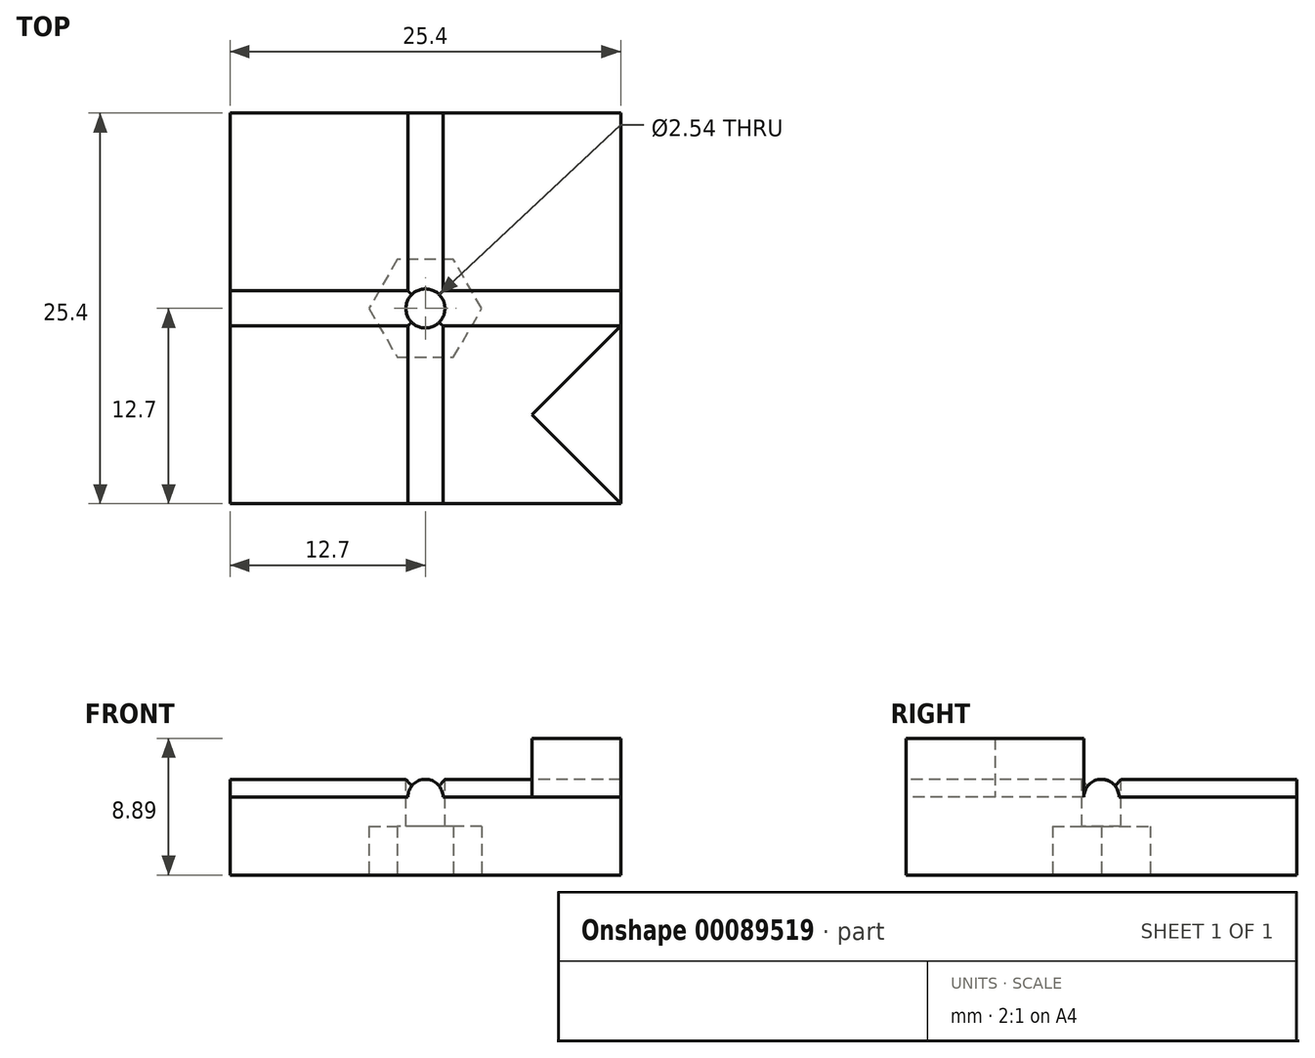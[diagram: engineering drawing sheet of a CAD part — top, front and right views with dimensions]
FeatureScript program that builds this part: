
annotation { "Feature Type Name" : "Feature", "Feature Type Description" : "" }
export const myFeature = defineFeature(function(context is Context, id is Id, definition is map)
    precondition{}
    {
        {
            var Q0;
            Q0=qCreatedBy(makeId("Top.planeOp"),FACE);
            var sketch = newSketch(context, id + "F0", { "sketchPlane" : qUnion([Q0])});
            skLineSegment(sketch, "E0.bottom", {"start": v(12.7, 12.7) * mm, "end": v(-12.7, 12.7) * mm});
            skLineSegment(sketch, "E0.top", {"start": v(12.7, -12.7) * mm, "end": v(-12.7, -12.7) * mm});
            skLineSegment(sketch, "E0.left", {"start": v(12.7, 12.7) * mm, "end": v(12.7, -12.7) * mm});
            skLineSegment(sketch, "E0.right", {"start": v(-12.7, 12.7) * mm, "end": v(-12.7, -12.7) * mm});
            skPoint(sketch, "E0.middle", {"position": v(0, 0) * mm});
            skSolve(sketch);
        }
        {
            var Q0;
            Q0=makeQuery(id+"F0.imprint","IMPRINT",FACE,{"disambiguationData":[TD([[makeQuery(id+"F0.imprint","IMPRINT",EDGE,{"derivedFrom":sQuery(id+"F0.wireOp",EDGE,"E0.bottom")}),1.0]])]});
            extrude(context, id + "F1", {"entities" : qUnion([Q0]), "depth" : 5.08 * mm});
        }
        {
            var Q0;
            Q0=makeQuery(id+"F1.opExtrude","SWEPT_FACE",FACE,{"disambiguationData":[OSD([sQuery(id+"F0.wireOp",EDGE,"E0.right")])]});
            var sketch = newSketch(context, id + "F2", { "sketchPlane" : qUnion([Q0])});
            skCircle(sketch, "E1", {"center": v(0, 5.08) * mm, "radius": 1.14 * mm});
            skSolve(sketch);
        }
        {
            var Q0;
            {var subQ0=sQuery(id+"F2.wireOp",EDGE,"E1");var subQ1=makeQuery(id+"F1.opExtrude","CAP_EDGE",EDGE,{"disambiguationData":[OSD([sQuery(id+"F0.wireOp",EDGE,"E0.right")])],"isStart":false});var subQ2=makeQuery(id+"F2.imprint","INTERSECT",VERTEX,{"disambiguationData":[OD(0.0)],"derivedFrom":[subQ1,subQ0]});Q0=makeQuery(id+"F2.imprint","IMPRINT",FACE,{"disambiguationData":[TD([[makeQuery(id+"F2.imprint","IMPRINT",EDGE,{"disambiguationData":[TD([[subQ2,1.0]])],"derivedFrom":subQ0}),1.0]])]});}
            extrude(context, id + "F3", {"entities" : qUnion([Q0]), "operationType" : NewBodyOperationType.ADD, "oppositeDirection" : true, "depth" : 25.4 * mm});
        }
        {
            var Q0;
            Q0=makeQuery(id+"F1.opExtrude","SWEPT_FACE",FACE,{"disambiguationData":[OSD([sQuery(id+"F0.wireOp",EDGE,"E0.top")])]});
            var sketch = newSketch(context, id + "F4", { "sketchPlane" : qUnion([Q0])});
            skCircle(sketch, "E2", {"center": v(0, 5.08) * mm, "radius": 1.14 * mm});
            skSolve(sketch);
        }
        {
            var Q0;
            {var subQ0=sQuery(id+"F4.wireOp",EDGE,"E2");var subQ1=makeQuery(id+"F1.opExtrude","CAP_EDGE",EDGE,{"disambiguationData":[OSD([sQuery(id+"F0.wireOp",EDGE,"E0.top")])],"isStart":false});var subQ2=makeQuery(id+"F4.imprint","INTERSECT",VERTEX,{"disambiguationData":[OD(0.0)],"derivedFrom":[subQ1,subQ0]});Q0=makeQuery(id+"F4.imprint","IMPRINT",FACE,{"disambiguationData":[TD([[makeQuery(id+"F4.imprint","IMPRINT",EDGE,{"disambiguationData":[TD([[subQ2,-1.0]])],"derivedFrom":subQ0}),1.0]])]});}
            extrude(context, id + "F5", {"entities" : qUnion([Q0]), "operationType" : NewBodyOperationType.ADD, "oppositeDirection" : true, "depth" : 25.4 * mm});
        }
        {
            var Q0;
            {var subQ1=sQuery(id+"F0.wireOp",EDGE,"E0.right");var subQ4=sQuery(id+"F0.wireOp",EDGE,"E0.left");var subQ5=makeQuery(id+"F1.opExtrude","SWEPT_FACE",FACE,{"disambiguationData":[OSD([subQ4])]});var subQ6=sQuery(id+"F0.wireOp",EDGE,"E0.top");var subQ7=makeQuery(id+"F1.opExtrude","SWEPT_FACE",FACE,{"disambiguationData":[OSD([subQ6])]});Q0=makeQuery(id+"F5.boolean.opBoolean","SPLIT",FACE,{"disambiguationData":[TD([subQ5])],"derivedFrom":makeQuery(id+"F3.boolean.opBoolean","SPLIT",FACE,{"disambiguationData":[TD([subQ7])],"derivedFrom":makeQuery(id+"F1.opExtrude","CAP_FACE",FACE,{"disambiguationData":[OSD([sQuery(id+"F0.wireOp",EDGE,"E0.bottom"),subQ6,subQ4,subQ1])],"isStart":false})})});}
            var sketch = newSketch(context, id + "F6", { "sketchPlane" : qUnion([Q0])});
            skCircle(sketch, "E3", {"center": v(0, 0) * mm, "radius": 1.27 * mm});
            skSolve(sketch);
        }
        {
            var Q0;
            Q0 = qSketchRegion(id + "F6", true);
            extrude(context, id + "F7", {"entities" : qUnion([Q0]), "operationType" : NewBodyOperationType.REMOVE, "oppositeDirection" : true, "depth" : 25.4 * mm, "hasSecondDirection" : true, "secondDirectionOppositeDirection" : false, "secondDirectionDepth" : 25.4 * mm});
        }
        {
            var Q0;
            {var subQ1=sQuery(id+"F0.wireOp",EDGE,"E0.right");var subQ4=sQuery(id+"F0.wireOp",EDGE,"E0.left");var subQ5=makeQuery(id+"F1.opExtrude","SWEPT_FACE",FACE,{"disambiguationData":[OSD([subQ4])]});var subQ6=sQuery(id+"F0.wireOp",EDGE,"E0.top");var subQ7=makeQuery(id+"F1.opExtrude","SWEPT_FACE",FACE,{"disambiguationData":[OSD([subQ6])]});Q0=makeQuery(id+"F5.boolean.opBoolean","SPLIT",FACE,{"disambiguationData":[TD([subQ5])],"derivedFrom":makeQuery(id+"F3.boolean.opBoolean","SPLIT",FACE,{"disambiguationData":[TD([subQ7])],"derivedFrom":makeQuery(id+"F1.opExtrude","CAP_FACE",FACE,{"disambiguationData":[OSD([sQuery(id+"F0.wireOp",EDGE,"E0.bottom"),subQ6,subQ4,subQ1])],"isStart":false})})});}
            var sketch = newSketch(context, id + "F8", { "sketchPlane" : qUnion([Q0])});
            skLineSegment(sketch, "E4", {"start": v(6.92, -6.92) * mm, "end": v(12.7, -12.7) * mm});
            skLineSegment(sketch, "E5", {"start": v(12.7, -1.14) * mm, "end": v(6.92, -6.92) * mm});
            skPoint(sketch, "E6.orphan", {"position": v(1.14, -1.14) * mm});
            skLineSegment(sketch, "E7", {"start": v(12.7, -12.7) * mm, "end": v(12.7, -1.14) * mm});
            skSolve(sketch);
        }
        {
            var Q0;
            Q0=makeQuery(id+"F8.imprint","IMPRINT",FACE,{"disambiguationData":[TD([[makeQuery(id+"F8.imprint","IMPRINT",EDGE,{"derivedFrom":sQuery(id+"F8.wireOp",EDGE,"E4")}),1.0]])]});
            extrude(context, id + "F9", {"entities" : qUnion([Q0]), "operationType" : NewBodyOperationType.ADD, "depth" : 3.8 * mm});
        }
        {
            var Q0;
            Q0=makeQuery(id+"F1.opExtrude","CAP_FACE",FACE,{"disambiguationData":[OSD([sQuery(id+"F0.wireOp",EDGE,"E0.bottom"),sQuery(id+"F0.wireOp",EDGE,"E0.top"),sQuery(id+"F0.wireOp",EDGE,"E0.left"),sQuery(id+"F0.wireOp",EDGE,"E0.right")])],"isStart":true});
            var sketch = newSketch(context, id + "F10", { "sketchPlane" : qUnion([Q0])});
            skCircle(sketch, "E8.cCircle", {"center": v(0, 0) * mm, "radius": 3.18 * mm, "construction": true});
            skLineSegment(sketch, "E8.0", {"start": v(1.83, -3.18) * mm, "end": v(-1.83, -3.18) * mm});
            skLineSegment(sketch, "E8.1", {"start": v(-1.83, -3.18) * mm, "end": v(-3.67, 0) * mm});
            skLineSegment(sketch, "E8.2", {"start": v(-3.67, 0) * mm, "end": v(-1.83, 3.17) * mm});
            skLineSegment(sketch, "E8.3", {"start": v(-1.83, 3.17) * mm, "end": v(1.83, 3.18) * mm});
            skLineSegment(sketch, "E8.4", {"start": v(1.83, 3.18) * mm, "end": v(3.67, 0) * mm});
            skLineSegment(sketch, "E8.5", {"start": v(3.67, 0) * mm, "end": v(1.83, -3.18) * mm});
            skPoint(sketch, "E8.0.midPoint", {"position": v(0, -3.18) * mm});
            skSolve(sketch);
        }
        {
            var Q0;
            Q0=makeQuery(id+"F10.imprint","IMPRINT",FACE,{"disambiguationData":[TD([[makeQuery(id+"F10.imprint","IMPRINT",EDGE,{"derivedFrom":sQuery(id+"F10.wireOp",EDGE,"E8.0")}),-1.0]])]});
            extrude(context, id + "F11", {"entities" : qUnion([Q0]), "operationType" : NewBodyOperationType.REMOVE, "oppositeDirection" : true, "depth" : 3.17 * mm});
        }
    });
